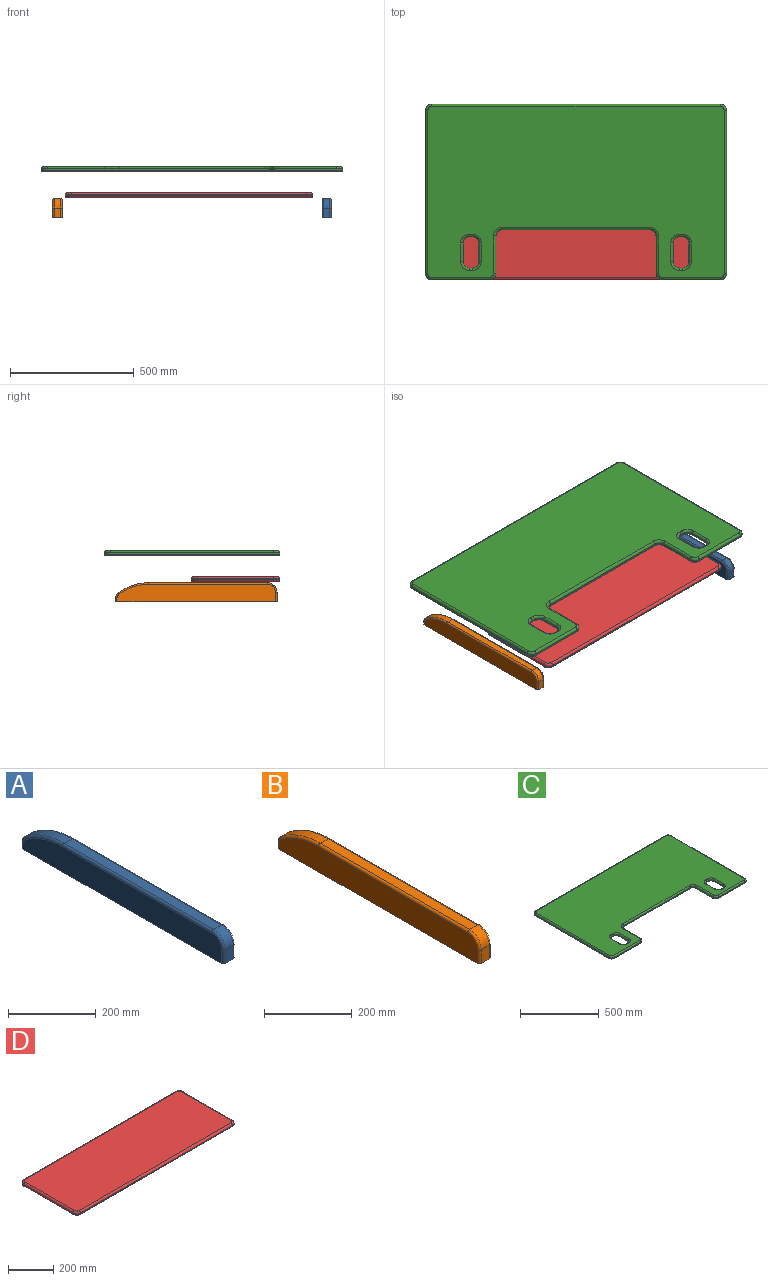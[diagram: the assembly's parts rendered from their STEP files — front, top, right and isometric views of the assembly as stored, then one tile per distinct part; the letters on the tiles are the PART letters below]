
ASSEMBLY  parts=4 mates=3
PART A: 21 faces, bbox 38.1x659.3x92.9 mm
  f0: plane 38.1x25.4mm, normal (0,-1,0), area 967.7mm2, adj f1,f7,f9,f15
  f1: plane 654.05x38.1mm, normal (0,0,-1), area 24884.7mm2, adj f0,f2,f5,f6,f9,f14,f15,f20
  f2: plane 25.4x13.47mm, normal (0,1,0), area 342.1mm2, adj f1,f8,f14,f20
  f3: cylinder r=203.2mm len=124.58mm, axis (-1,0,0), area 3406.2mm2, adj f4,f8,f12,f18
  f4: plane 481.55x25.4mm, normal (0,0,1), area 12231.3mm2, adj f3,f7,f11,f17
  f5: plane 641.35x69.85mm, normal (1,0,0), area 42657.8mm2, adj f1,f9,f10,f11,f12,f13,f14
  f6: plane 641.35x69.85mm, normal (-1,0,0), area 42657.8mm2, adj f1,f15,f16,f17,f18,f19,f20
  f7: cylinder r=38.1mm len=38.1mm, axis (-1,0,0), area 1520.1mm2, adj f0,f4,f10,f16
  f8: cylinder r=25.4mm len=25.4mm, axis (-1,0,0), area 587.6mm2, adj f2,f3,f13,f19
  f9: cylinder r=6.35mm len=38.1mm, axis (0,0,1), area 380mm2, adj f0,f1,f5,f10
  f10: torus R=31.75mm, axis (1,0,0), area 560.8mm2, adj f5,f7,f9,f11
  f11: cylinder r=6.35mm len=481.55mm, axis (0,1,0), area 4803.2mm2, adj f4,f5,f10,f12
  f12: torus R=196.85mm, axis (1,0,0), area 1322.4mm2, adj f3,f5,f11,f13
  f13: torus R=19.05mm, axis (1,0,0), area 209.8mm2, adj f5,f8,f12,f14
  f14: cylinder r=6.35mm len=13.47mm, axis (0,0,-1), area 134.3mm2, adj f1,f2,f5,f13
  f15: cylinder r=6.35mm len=38.1mm, axis (0,0,-1), area 380mm2, adj f0,f1,f6,f16
  f16: torus R=31.75mm, axis (1,0,0), area 560.8mm2, adj f6,f7,f15,f17
  f17: cylinder r=6.35mm len=481.55mm, axis (0,-1,0), area 4803.2mm2, adj f4,f6,f16,f18
  f18: torus R=196.85mm, axis (1,0,0), area 1322.4mm2, adj f3,f6,f17,f19
  f19: torus R=19.05mm, axis (1,0,0), area 209.8mm2, adj f6,f8,f18,f20
  f20: cylinder r=6.35mm len=13.47mm, axis (0,0,1), area 134.3mm2, adj f1,f2,f6,f19
PART B: 21 faces, bbox 38.1x659.5x92.9 mm
  f0: plane 38.1x25.4mm, normal (0,-1,0), area 967.7mm2, adj f1,f7,f9,f15
  f1: plane 654.3x38.1mm, normal (0,0,-1), area 24894.4mm2, adj f0,f2,f5,f6,f9,f14,f15,f20
  f2: plane 25.4x13.47mm, normal (0,1,0), area 342.1mm2, adj f1,f8,f14,f20
  f3: cylinder r=203.2mm len=124.58mm, axis (-1,0,0), area 3406.2mm2, adj f4,f8,f12,f18
  f4: plane 481.8x25.4mm, normal (0,0,1), area 12237.7mm2, adj f3,f7,f11,f17
  f5: plane 641.6x69.85mm, normal (1,0,0), area 42675.5mm2, adj f1,f9,f10,f11,f12,f13,f14
  f6: plane 641.6x69.85mm, normal (-1,0,0), area 42675.5mm2, adj f1,f15,f16,f17,f18,f19,f20
  f7: cylinder r=38.1mm len=38.1mm, axis (-1,0,0), area 1520.1mm2, adj f0,f4,f10,f16
  f8: cylinder r=25.4mm len=25.4mm, axis (-1,0,0), area 587.6mm2, adj f2,f3,f13,f19
  f9: cylinder r=6.35mm len=38.1mm, axis (0,0,1), area 380mm2, adj f0,f1,f5,f10
  f10: torus R=31.75mm, axis (1,0,0), area 560.8mm2, adj f5,f7,f9,f11
  f11: cylinder r=6.35mm len=481.8mm, axis (0,1,0), area 4805.7mm2, adj f4,f5,f10,f12
  f12: torus R=196.85mm, axis (1,0,0), area 1322.4mm2, adj f3,f5,f11,f13
  f13: torus R=19.05mm, axis (1,0,0), area 209.8mm2, adj f5,f8,f12,f14
  f14: cylinder r=6.35mm len=13.47mm, axis (0,0,-1), area 134.3mm2, adj f1,f2,f5,f13
  f15: cylinder r=6.35mm len=38.1mm, axis (0,0,-1), area 380mm2, adj f0,f1,f6,f16
  f16: torus R=31.75mm, axis (1,0,0), area 560.8mm2, adj f6,f7,f15,f17
  f17: cylinder r=6.35mm len=481.8mm, axis (0,-1,0), area 4805.7mm2, adj f4,f6,f16,f18
  f18: torus R=196.85mm, axis (1,0,0), area 1322.4mm2, adj f3,f6,f17,f19
  f19: torus R=19.05mm, axis (1,0,0), area 209.8mm2, adj f6,f8,f18,f20
  f20: cylinder r=6.35mm len=13.47mm, axis (0,0,1), area 134.3mm2, adj f1,f2,f6,f19
PART C: 98 faces, bbox 1223.4x715.4x19.1 mm
  f0: plane 1200.15x692.15mm, normal (0,0,1), area 673380.5mm2, adj f18,f19,f20,f21,f22,f23,f24,f25
  f1: plane 1212.85x704.85mm, normal (0,0,-1), area 702129.2mm2, adj f34,f35,f36,f37,f38,f39,f40,f41
  f2: plane 596.9x6.35mm, normal (0,-1,0), area 3790.3mm2, adj f10,f11,f29,f37
  f3: plane 152.4x6.35mm, normal (-1,0,0), area 967.7mm2, adj f10,f12,f25,f41
  f4: plane 234.95x6.35mm, normal (0,-1,0), area 1491.9mm2, adj f12,f14,f21,f45
  f5: plane 660.4x6.35mm, normal (1,0,0), area 4193.5mm2, adj f14,f15,f18,f49
  f6: plane 1168.4x6.35mm, normal (0,1,0), area 7419.3mm2, adj f15,f16,f22,f46
  f7: plane 660.4x6.35mm, normal (-1,0,0), area 4193.5mm2, adj f16,f17,f26,f42
  f8: plane 234.95x6.35mm, normal (0,-1,0), area 1491.9mm2, adj f13,f17,f30,f38
  f9: plane 152.4x6.35mm, normal (1,0,0), area 967.7mm2, adj f11,f13,f33,f34
  f10: cylinder r=25.4mm len=25.4mm, axis (0,0,-1), area 253.4mm2, adj f2,f3,f27,f39
  f11: cylinder r=25.4mm len=25.4mm, axis (0,0,1), area 253.4mm2, adj f2,f9,f31,f35
  f12: cylinder r=25.4mm len=25.4mm, axis (0,0,-1), area 253.4mm2, adj f3,f4,f23,f43
  f13: cylinder r=25.4mm len=25.4mm, axis (0,0,-1), area 253.4mm2, adj f8,f9,f32,f36
  f14: cylinder r=25.4mm len=25.4mm, axis (0,0,-1), area 253.4mm2, adj f4,f5,f19,f47
  f15: cylinder r=25.4mm len=25.4mm, axis (0,0,-1), area 253.4mm2, adj f5,f6,f20,f48
  f16: cylinder r=25.4mm len=25.4mm, axis (0,0,1), area 253.4mm2, adj f6,f7,f24,f44
  f17: cylinder r=25.4mm len=25.4mm, axis (0,0,-1), area 253.4mm2, adj f7,f8,f28,f40
  f18: cylinder r=9.53mm len=660.4mm, axis (0,-1,0), area 9880.8mm2, adj f0,f5,f19,f20
  f19: torus R=15.88mm, axis (0,0,1), area 515.6mm2, adj f0,f14,f18,f21
  f20: torus R=15.88mm, axis (0,0,1), area 515.6mm2, adj f0,f15,f18,f22
  f21: cylinder r=9.53mm len=234.95mm, axis (-1,0,0), area 3515.3mm2, adj f0,f4,f19,f23
  f22: cylinder r=9.53mm len=1168.4mm, axis (1,0,0), area 17481.4mm2, adj f0,f6,f20,f24
  f23: torus R=15.88mm, axis (0,0,1), area 515.6mm2, adj f0,f12,f21,f25
  f24: torus R=15.88mm, axis (0,0,1), area 515.6mm2, adj f0,f16,f22,f26
  f25: cylinder r=9.53mm len=152.4mm, axis (0,1,0), area 2280.2mm2, adj f0,f3,f23,f27
  f26: cylinder r=9.53mm len=660.4mm, axis (0,1,0), area 9880.8mm2, adj f0,f7,f24,f28
  f27: torus R=34.92mm, axis (0,0,1), area 678.3mm2, adj f0,f10,f25,f29
  f28: torus R=15.88mm, axis (0,0,1), area 515.6mm2, adj f0,f17,f26,f30
  f29: cylinder r=9.53mm len=596.9mm, axis (-1,0,0), area 8930.7mm2, adj f0,f2,f27,f31
  f30: cylinder r=9.53mm len=234.95mm, axis (-1,0,0), area 3515.3mm2, adj f0,f8,f28,f32
  f31: torus R=34.92mm, axis (0,0,1), area 678.3mm2, adj f0,f11,f29,f33
  f32: torus R=15.88mm, axis (0,0,1), area 515.6mm2, adj f0,f13,f30,f33
  f33: cylinder r=9.53mm len=152.4mm, axis (0,-1,0), area 2280.2mm2, adj f0,f9,f31,f32
  f34: cylinder r=3.17mm len=152.4mm, axis (0,1,0), area 760.1mm2, adj f1,f9,f35,f36
  f35: torus R=28.57mm, axis (0,0,1), area 208mm2, adj f1,f11,f34,f37
  f36: torus R=22.23mm, axis (0,0,1), area 189.9mm2, adj f1,f13,f34,f38
  f37: cylinder r=3.17mm len=596.9mm, axis (1,0,0), area 2976.9mm2, adj f1,f2,f35,f39
  f38: cylinder r=3.17mm len=234.95mm, axis (1,0,0), area 1171.8mm2, adj f1,f8,f36,f40
  f39: torus R=28.57mm, axis (0,0,1), area 208mm2, adj f1,f10,f37,f41
  f40: torus R=22.23mm, axis (0,0,1), area 189.9mm2, adj f1,f17,f38,f42
  f41: cylinder r=3.17mm len=152.4mm, axis (0,-1,0), area 760.1mm2, adj f1,f3,f39,f43
  f42: cylinder r=3.17mm len=660.4mm, axis (0,-1,0), area 3293.6mm2, adj f1,f7,f40,f44
  f43: torus R=22.23mm, axis (0,0,1), area 189.9mm2, adj f1,f12,f41,f45
  f44: torus R=22.23mm, axis (0,0,1), area 189.9mm2, adj f1,f16,f42,f46
  f45: cylinder r=3.17mm len=234.95mm, axis (1,0,0), area 1171.8mm2, adj f1,f4,f43,f47
  f46: cylinder r=3.17mm len=1168.4mm, axis (-1,0,0), area 5827.1mm2, adj f1,f6,f44,f48
  f47: torus R=22.23mm, axis (0,0,1), area 189.9mm2, adj f1,f14,f45,f49
  f48: torus R=22.23mm, axis (0,0,1), area 189.9mm2, adj f1,f15,f46,f49
  f49: cylinder r=3.17mm len=660.4mm, axis (0,1,0), area 3293.6mm2, adj f1,f5,f47,f48
  f50: plane 12.7x3.18mm, normal (0,-1,0), area 40.3mm2, adj f58,f61,f77,f93
  f51: plane 76.2x3.18mm, normal (1,0,0), area 241.9mm2, adj f58,f59,f74,f90
  f52: plane 12.7x3.18mm, normal (0,1,0), area 40.3mm2, adj f59,f60,f78,f94
  f53: plane 76.2x3.18mm, normal (-1,0,0), area 241.9mm2, adj f60,f61,f81,f97
  f54: plane 12.7x3.18mm, normal (0,-1,0), area 40.3mm2, adj f62,f65,f69,f85
  f55: plane 76.2x3.18mm, normal (1,0,0), area 241.9mm2, adj f64,f65,f66,f82
  f56: plane 12.7x3.18mm, normal (0,1,0), area 40.3mm2, adj f63,f64,f70,f86
  f57: plane 76.2x3.18mm, normal (-1,0,0), area 241.9mm2, adj f62,f63,f73,f89
  f58: cylinder r=25.4mm len=25.4mm, axis (0,0,-1), area 126.7mm2, adj f50,f51,f75,f91
  f59: cylinder r=25.4mm len=25.4mm, axis (0,0,1), area 126.7mm2, adj f51,f52,f76,f92
  f60: cylinder r=25.4mm len=25.4mm, axis (0,0,-1), area 126.7mm2, adj f52,f53,f80,f96
  f61: cylinder r=25.4mm len=25.4mm, axis (0,0,1), area 126.7mm2, adj f50,f53,f79,f95
  f62: cylinder r=25.4mm len=25.4mm, axis (0,0,-1), area 126.7mm2, adj f54,f57,f71,f87
  f63: cylinder r=25.4mm len=25.4mm, axis (0,0,1), area 126.7mm2, adj f56,f57,f72,f88
  f64: cylinder r=25.4mm len=25.4mm, axis (0,0,-1), area 126.7mm2, adj f55,f56,f68,f84
  f65: cylinder r=25.4mm len=25.4mm, axis (0,0,1), area 126.7mm2, adj f54,f55,f67,f83
  f66: cylinder r=9.53mm len=76.2mm, axis (0,1,0), area 1140.1mm2, adj f0,f55,f67,f68
  f67: torus R=34.92mm, axis (0,0,1), area 678.3mm2, adj f0,f65,f66,f69
  f68: torus R=34.92mm, axis (0,0,1), area 678.3mm2, adj f0,f64,f66,f70
  f69: cylinder r=9.53mm len=12.7mm, axis (1,0,0), area 190mm2, adj f0,f54,f67,f71
  f70: cylinder r=9.53mm len=12.7mm, axis (-1,0,0), area 190mm2, adj f0,f56,f68,f72
  f71: torus R=34.92mm, axis (0,0,1), area 678.3mm2, adj f0,f62,f69,f73
  f72: torus R=34.92mm, axis (0,0,1), area 678.3mm2, adj f0,f63,f70,f73
  f73: cylinder r=9.53mm len=76.2mm, axis (0,-1,0), area 1140.1mm2, adj f0,f57,f71,f72
  f74: cylinder r=9.53mm len=76.2mm, axis (0,1,0), area 1140.1mm2, adj f0,f51,f75,f76
  f75: torus R=34.92mm, axis (0,0,1), area 678.3mm2, adj f0,f58,f74,f77
  f76: torus R=34.92mm, axis (0,0,1), area 678.3mm2, adj f0,f59,f74,f78
  f77: cylinder r=9.53mm len=12.7mm, axis (1,0,0), area 190mm2, adj f0,f50,f75,f79
  f78: cylinder r=9.53mm len=12.7mm, axis (-1,0,0), area 190mm2, adj f0,f52,f76,f80
  f79: torus R=34.92mm, axis (0,0,1), area 678.3mm2, adj f0,f61,f77,f81
  f80: torus R=34.92mm, axis (0,0,1), area 678.3mm2, adj f0,f60,f78,f81
  f81: cylinder r=9.53mm len=76.2mm, axis (0,-1,0), area 1140.1mm2, adj f0,f53,f79,f80
  f82: cylinder r=6.35mm len=76.2mm, axis (0,-1,0), area 760.1mm2, adj f1,f55,f83,f84
  f83: torus R=31.75mm, axis (0,0,1), area 434.1mm2, adj f1,f65,f82,f85
  f84: torus R=31.75mm, axis (0,0,1), area 434.1mm2, adj f1,f64,f82,f86
  f85: cylinder r=6.35mm len=12.7mm, axis (-1,0,0), area 126.7mm2, adj f1,f54,f83,f87
  f86: cylinder r=6.35mm len=12.7mm, axis (1,0,0), area 126.7mm2, adj f1,f56,f84,f88
  f87: torus R=31.75mm, axis (0,0,1), area 434.1mm2, adj f1,f62,f85,f89
  f88: torus R=31.75mm, axis (0,0,1), area 434.1mm2, adj f1,f63,f86,f89
  f89: cylinder r=6.35mm len=76.2mm, axis (0,1,0), area 760.1mm2, adj f1,f57,f87,f88
  f90: cylinder r=6.35mm len=76.2mm, axis (0,-1,0), area 760.1mm2, adj f1,f51,f91,f92
  f91: torus R=31.75mm, axis (0,0,1), area 434.1mm2, adj f1,f58,f90,f93
  f92: torus R=31.75mm, axis (0,0,1), area 434.1mm2, adj f1,f59,f90,f94
  f93: cylinder r=6.35mm len=12.7mm, axis (-1,0,0), area 126.7mm2, adj f1,f50,f91,f95
  f94: cylinder r=6.35mm len=12.7mm, axis (1,0,0), area 126.7mm2, adj f1,f52,f92,f96
  f95: torus R=31.75mm, axis (0,0,1), area 434.1mm2, adj f1,f61,f93,f97
  f96: torus R=31.75mm, axis (0,0,1), area 434.1mm2, adj f1,f60,f94,f97
  f97: cylinder r=6.35mm len=76.2mm, axis (0,1,0), area 760.1mm2, adj f1,f53,f95,f96
PART D: 26 faces, bbox 1007.5x363x19.1 mm
  f0: plane 307.98x3.18mm, normal (1,0,0), area 977.8mm2, adj f6,f9,f15,f24
  f1: plane 952.5x3.18mm, normal (0,1,0), area 3024.2mm2, adj f6,f7,f16,f23
  f2: plane 307.98x3.18mm, normal (-1,0,0), area 977.8mm2, adj f7,f8,f12,f19
  f3: plane 952.5x3.18mm, normal (0,-1,0), area 3024.2mm2, adj f8,f9,f11,f20
  f4: plane 984.25x339.73mm, normal (0,0,1), area 334158mm2, adj f10,f11,f12,f13,f14,f15,f16,f17
  f5: plane 990.6x346.08mm, normal (0,0,-1), area 342510.4mm2, adj f18,f19,f20,f21,f22,f23,f24,f25
  f6: cylinder r=25.4mm len=25.4mm, axis (0,0,1), area 126.7mm2, adj f0,f1,f17,f25
  f7: cylinder r=25.4mm len=25.4mm, axis (0,0,-1), area 126.7mm2, adj f1,f2,f14,f21
  f8: cylinder r=25.4mm len=25.4mm, axis (0,0,1), area 126.7mm2, adj f2,f3,f10,f18
  f9: cylinder r=25.4mm len=25.4mm, axis (0,0,-1), area 126.7mm2, adj f0,f3,f13,f22
  f10: torus R=15.88mm, axis (0,0,1), area 515.6mm2, adj f4,f8,f11,f12
  f11: cylinder r=9.53mm len=952.5mm, axis (-1,0,0), area 14251.1mm2, adj f3,f4,f10,f13
  f12: cylinder r=9.53mm len=307.98mm, axis (0,1,0), area 4607.9mm2, adj f2,f4,f10,f14
  f13: torus R=15.88mm, axis (0,0,1), area 515.6mm2, adj f4,f9,f11,f15
  f14: torus R=15.88mm, axis (0,0,1), area 515.6mm2, adj f4,f7,f12,f16
  f15: cylinder r=9.53mm len=307.98mm, axis (0,-1,0), area 4607.9mm2, adj f0,f4,f13,f17
  f16: cylinder r=9.53mm len=952.5mm, axis (1,0,0), area 14251.1mm2, adj f1,f4,f14,f17
  f17: torus R=15.88mm, axis (0,0,1), area 515.6mm2, adj f4,f6,f15,f16
  f18: torus R=19.05mm, axis (0,0,1), area 361.8mm2, adj f5,f8,f19,f20
  f19: cylinder r=6.35mm len=307.98mm, axis (0,-1,0), area 3071.9mm2, adj f2,f5,f18,f21
  f20: cylinder r=6.35mm len=952.5mm, axis (1,0,0), area 9500.8mm2, adj f3,f5,f18,f22
  f21: torus R=19.05mm, axis (0,0,1), area 361.8mm2, adj f5,f7,f19,f23
  f22: torus R=19.05mm, axis (0,0,1), area 361.8mm2, adj f5,f9,f20,f24
  f23: cylinder r=6.35mm len=952.5mm, axis (-1,0,0), area 9500.8mm2, adj f1,f5,f21,f25
  f24: cylinder r=6.35mm len=307.98mm, axis (0,1,0), area 3071.9mm2, adj f0,f5,f22,f25
  f25: torus R=19.05mm, axis (0,0,1), area 361.8mm2, adj f5,f6,f23,f24
PLACE A t=(484.59,-191.89,-85.06)mm
PLACE B t=(-605.65,-191.89,-85.06)mm
PLACE C t=(-41.7,-0.13,102.6)mm
PLACE D t=(-53.77,-23.94,-3.12)mm
MATE planar B.f1 <-> A.f9  axis (0,0,-1) through (-586.6,135.26,-85.06)mm
MATE parallel D.f3 <-> C.f8  axis (0,-1,0) through (-53.77,-203.33,4.81)mm
MATE planar B.f0 <-> A.f0  axis (0,-1,0) through (-586.6,-191.89,-66.01)mm
